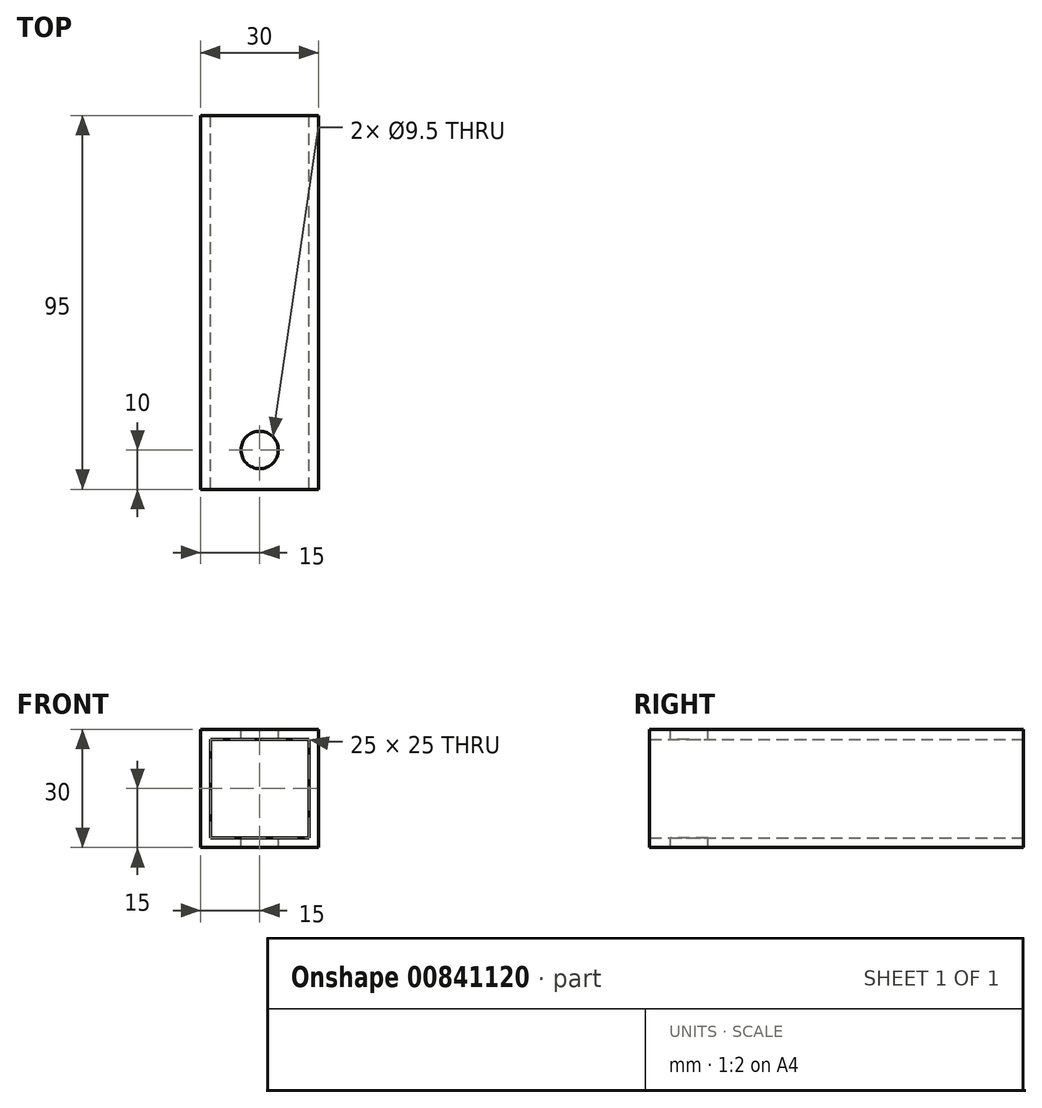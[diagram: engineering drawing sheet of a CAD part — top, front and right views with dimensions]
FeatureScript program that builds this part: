
annotation { "Feature Type Name" : "Feature", "Feature Type Description" : "" }
export const myFeature = defineFeature(function(context is Context, id is Id, definition is map)
    precondition{}
    {
        {
            var Q0;
            Q0=qCreatedBy(makeId("Front.planeOp"),FACE);
            var sketch = newSketch(context, id + "F0", { "sketchPlane" : qUnion([Q0])});
            skLineSegment(sketch, "E0.bottom", {"start": v(15, 15) * mm, "end": v(-15, 15) * mm});
            skLineSegment(sketch, "E0.top", {"start": v(15, -15) * mm, "end": v(-15, -15) * mm});
            skLineSegment(sketch, "E0.left", {"start": v(15, 15) * mm, "end": v(15, -15) * mm});
            skLineSegment(sketch, "E0.right", {"start": v(-15, 15) * mm, "end": v(-15, -15) * mm});
            skPoint(sketch, "E0.middle", {"position": v(0, 0) * mm});
            skSolve(sketch);
        }
        {
            var Q0;
            Q0=qSketchRegion(id+"F0",true);
            extrude(context, id + "F1", {"entities" : qUnion([Q0]), "depth" : 95 * mm, "offsetDistance" : 25 * mm});
        }
        {
            var Q0;
            Q0=makeQuery(id+"F1.opExtrude","CAP_FACE",FACE,{"disambiguationData":[OSD([sQuery(id+"F0.wireOp",EDGE,"E0.bottom"),sQuery(id+"F0.wireOp",EDGE,"E0.top"),sQuery(id+"F0.wireOp",EDGE,"E0.left"),sQuery(id+"F0.wireOp",EDGE,"E0.right")])],"isStart":false});
            var Q1;
            Q1=makeQuery(id+"F1.opExtrude","CAP_FACE",FACE,{"disambiguationData":[OSD([sQuery(id+"F0.wireOp",EDGE,"E0.bottom"),sQuery(id+"F0.wireOp",EDGE,"E0.top"),sQuery(id+"F0.wireOp",EDGE,"E0.left"),sQuery(id+"F0.wireOp",EDGE,"E0.right")])],"isStart":true});
            shell(context, id + "F2", {"entities" : qUnion([Q0, Q1]), "thickness" : 2.5 * mm});
        }
        {
            var Q0;
            Q0=makeQuery(id+"F1.opExtrude","SWEPT_FACE",FACE,{"disambiguationData":[OSD([sQuery(id+"F0.wireOp",EDGE,"E0.bottom")])]});
            var sketch = newSketch(context, id + "F3", { "sketchPlane" : qUnion([Q0])});
            skCircle(sketch, "E1", {"center": v(0, -85) * mm, "radius": 4.75 * mm});
            skPoint(sketch, "E1.centerSnap0", {"position": v(15, -85) * mm});
            skCircle(sketch, "E2", {"center": v(0, -70) * mm, "radius": 4.75 * mm, "construction": true});
            skSolve(sketch);
        }
        {
            var Q0;
            Q0=makeQuery(id+"F3.imprint","IMPRINT",FACE,{"disambiguationData":[TD([[makeQuery(id+"F3.imprint","IMPRINT",EDGE,{"derivedFrom":sQuery(id+"F3.wireOp",EDGE,"E1")}),1.0]])]});
            var Q1;
            Q1=makeQuery(id+"F3.imprint","IMPRINT",FACE,{"disambiguationData":[TD([[makeQuery(id+"F3.imprint","IMPRINT",EDGE,{"derivedFrom":sQuery(id+"F3.wireOp",EDGE,"E2")}),1.0]])]});
            extrude(context, id + "F4", {"entities" : qUnion([Q0, Q1]), "operationType" : NewBodyOperationType.REMOVE, "oppositeDirection" : true, "depth" : 33.1 * mm, "offsetDistance" : 25 * mm});
        }
    });
